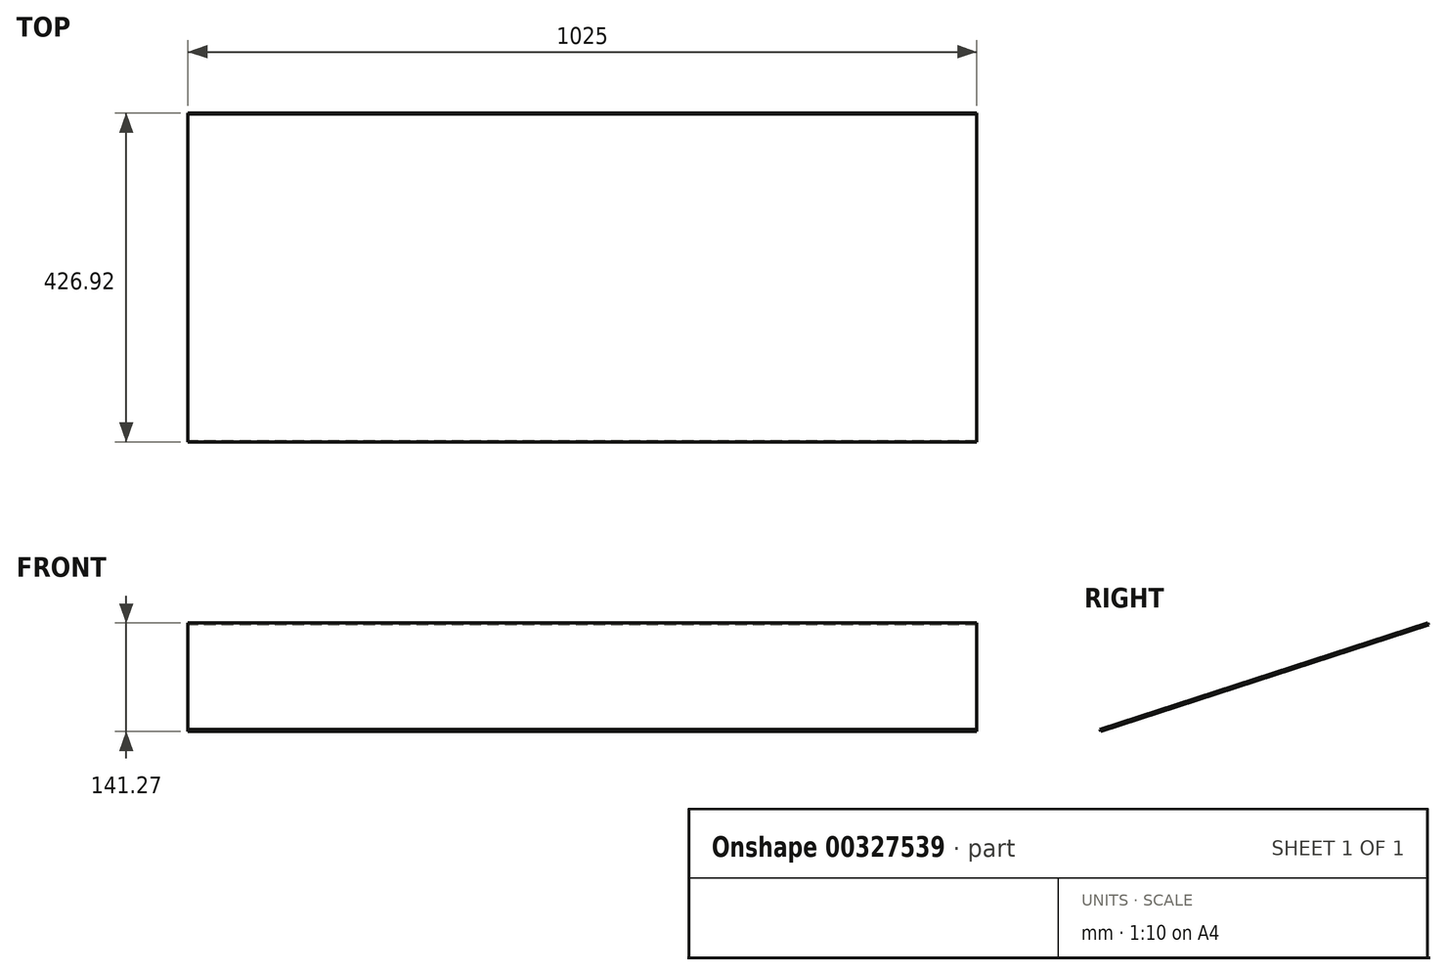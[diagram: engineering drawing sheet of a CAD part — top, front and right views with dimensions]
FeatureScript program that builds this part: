
annotation { "Feature Type Name" : "Feature", "Feature Type Description" : "" }
export const myFeature = defineFeature(function(context is Context, id is Id, definition is map)
    precondition{}
    {
        {
            var Q0;
            Q0=qCreatedBy(makeId("Right.planeOp"),FACE);
            var sketch = newSketch(context, id + "F0", { "sketchPlane" : qUnion([Q0])});
            skLineSegment(sketch, "E0", {"start": v(0, 0) * mm, "end": v(2288, 0) * mm});
            skLineSegment(sketch, "E1", {"start": v(2288, 0) * mm, "end": v(2288, 684.37) * mm});
            skLineSegment(sketch, "E2", {"start": v(2100, 0) * mm, "end": v(2100, 623.29) * mm});
            skLineSegment(sketch, "E3", {"start": v(2050, 0) * mm, "end": v(2050, 607.04) * mm});
            skLineSegment(sketch, "E4", {"start": v(2100, 623.29) * mm, "end": v(2288, 684.37) * mm});
            skLineSegment(sketch, "E5", {"start": v(2100, 623.29) * mm, "end": v(2050, 607.04) * mm});
            skLineSegment(sketch, "E6", {"start": v(2050, 607.04) * mm, "end": v(1862, 545.95) * mm});
            skLineSegment(sketch, "E7", {"start": v(2050, 607.04) * mm, "end": v(2041.35, 633.67) * mm});
            skLineSegment(sketch, "E8", {"start": v(2100, 623.29) * mm, "end": v(2091.35, 649.92) * mm});
            skLineSegment(sketch, "E9", {"start": v(2288, 684.37) * mm, "end": v(2279.35, 711) * mm});
            skLineSegment(sketch, "E10", {"start": v(2279.35, 711) * mm, "end": v(2091.35, 649.92) * mm});
            skLineSegment(sketch, "E11", {"start": v(2091.35, 649.92) * mm, "end": v(2041.35, 633.67) * mm});
            skLineSegment(sketch, "E12", {"start": v(2041.35, 633.67) * mm, "end": v(1853.35, 572.58) * mm});
            skLineSegment(sketch, "E13", {"start": v(1853.35, 572.58) * mm, "end": v(1862, 545.95) * mm});
            skLineSegment(sketch, "E14", {"start": v(1854.27, 569.73) * mm, "end": v(2280.27, 708.15) * mm});
            skSolve(sketch);
        }
        {
            var Q0;
            {var subQ0=sQuery(id+"F0.wireOp",EDGE,"0M8AAAyR-SB0r-MtMV-LE9l-MARlShi8dbRd");Q0=makeQuery(id+"F0.imprint","IMPRINT",FACE,{"disambiguationData":[TD([[makeQuery(id+"F0.imprint","IMPRINT",EDGE,{"derivedFrom":subQ0}),-1.0]])]});}
            var Q1;
            {var subQ0=sQuery(id+"F0.wireOp",EDGE,"1FGk7jgl-vVaA-wB1T-qpKy-0b2ghD9h8zY1");Q1=makeQuery(id+"F0.imprint","IMPRINT",FACE,{"disambiguationData":[TD([[makeQuery(id+"F0.imprint","IMPRINT",EDGE,{"derivedFrom":subQ0}),1.0]])]});}
            var Q2;
            {var subQ0=sQuery(id+"F0.wireOp",EDGE,"ccb0210a-ae8c-467c-bc7f-bc7526da68d5.trimOffspring");Q2=makeQuery(id+"F0.imprint","IMPRINT",FACE,{"disambiguationData":[TD([[makeQuery(id+"F0.imprint","IMPRINT",EDGE,{"derivedFrom":subQ0}),-1.0]])]});}
            var Q3;
            {var subQ0=sQuery(id+"F0.wireOp",EDGE,"E12");Q3=makeQuery(id+"F0.imprint","IMPRINT",FACE,{"disambiguationData":[TD([[makeQuery(id+"F0.imprint","IMPRINT",EDGE,{"derivedFrom":subQ0}),1.0]])]});}
            var Q4;
            {var subQ0=sQuery(id+"F0.wireOp",EDGE,"E11");Q4=makeQuery(id+"F0.imprint","IMPRINT",FACE,{"disambiguationData":[TD([[makeQuery(id+"F0.imprint","IMPRINT",EDGE,{"derivedFrom":subQ0}),1.0]])]});}
            var Q5;
            {var subQ0=sQuery(id+"F0.wireOp",EDGE,"E10");Q5=makeQuery(id+"F0.imprint","IMPRINT",FACE,{"disambiguationData":[TD([[makeQuery(id+"F0.imprint","IMPRINT",EDGE,{"derivedFrom":subQ0}),1.0]])]});}
            extrude(context, id + "F1", {"entities" : qUnion([Q0, Q1, Q2, Q3, Q4, Q5]), "depth" : 1100 * mm, "symmetric" : true});
        }
        {
            var Q0;
            Q0=makeQuery(id+"F1.opExtrude","SWEPT_FACE",FACE,{"disambiguationData":[OSD([sQuery(id+"F0.wireOp",EDGE,"E10"),sQuery(id+"F0.wireOp",EDGE,"E11"),sQuery(id+"F0.wireOp",EDGE,"E12")])]});
            var sketch = newSketch(context, id + "F2", { "sketchPlane" : qUnion([Q0])});
            skLineSegment(sketch, "E15", {"start": v(0, 2163.54) * mm, "end": v(500, 2163.54) * mm});
            skPoint(sketch, "E15.startSnap0", {"position": v(550, 2163.54) * mm});
            skPoint(sketch, "E15.startSnap1", {"position": v(0, 2387.5) * mm});
            skPoint(sketch, "E15.endSnap0", {"position": v(550, 2163.54) * mm});
            skLineSegment(sketch, "E16", {"start": v(500, 2188.54) * mm, "end": v(475, 2188.54) * mm});
            skLineSegment(sketch, "E17", {"start": v(475, 2188.54) * mm, "end": v(475, 2138.54) * mm});
            skLineSegment(sketch, "E18", {"start": v(475, 2138.54) * mm, "end": v(500, 2138.54) * mm});
            skLineSegment(sketch, "E19.bottom", {"start": v(462.5, 2387.5) * mm, "end": v(512.5, 2387.5) * mm});
            skLineSegment(sketch, "E19.top", {"start": v(462.5, 1939.58) * mm, "end": v(512.5, 1939.58) * mm});
            skLineSegment(sketch, "E19.left", {"start": v(462.5, 2387.5) * mm, "end": v(462.5, 1939.58) * mm});
            skLineSegment(sketch, "E19.right", {"start": v(512.5, 2387.5) * mm, "end": v(512.5, 1939.58) * mm});
            skPoint(sketch, "E19.middle", {"position": v(487.5, 2163.54) * mm});
            skPoint(sketch, "E19.middle.positionSnap0", {"position": v(487.5, 2138.54) * mm});
            skPoint(sketch, "E19.centerSnap0", {"position": v(487.5, 2138.54) * mm});
            skLineSegment(sketch, "E20.MirrorCS", {"start": v(0, 2163.54) * mm, "end": v(-500, 2163.54) * mm});
            skLineSegment(sketch, "E21.MirrorCS", {"start": v(-462.5, 2387.5) * mm, "end": v(-462.5, 1939.58) * mm});
            skLineSegment(sketch, "E22.MirrorCS", {"start": v(-475, 2188.54) * mm, "end": v(-475, 2138.54) * mm});
            skLineSegment(sketch, "E23.MirrorCS", {"start": v(-475, 2138.54) * mm, "end": v(-500, 2138.54) * mm});
            skLineSegment(sketch, "E24.MirrorCS", {"start": v(-500, 2138.54) * mm, "end": v(-500, 2163.54) * mm});
            skLineSegment(sketch, "E25.MirrorCS", {"start": v(-500, 2163.54) * mm, "end": v(-500, 2188.54) * mm});
            skLineSegment(sketch, "E26.MirrorCS", {"start": v(-500, 2188.54) * mm, "end": v(-475, 2188.54) * mm});
            skLineSegment(sketch, "E27.MirrorCS", {"start": v(-512.5, 2387.5) * mm, "end": v(-512.5, 1939.58) * mm});
            skLineSegment(sketch, "E28", {"start": v(500, 2138.54) * mm, "end": v(500, 2188.54) * mm});
            skSolve(sketch);
        }
        {
            var Q0;
            {var subQ0=sQuery(id+"F2.wireOp",EDGE,"E27.MirrorCS");Q0=makeQuery(id+"F2.imprint","IMPRINT",FACE,{"disambiguationData":[TD([[makeQuery(id+"F2.imprint","IMPRINT",EDGE,{"derivedFrom":subQ0}),-1.0]])]});}
            var Q1;
            {var subQ0=sQuery(id+"F2.wireOp",EDGE,"E19.right");Q1=makeQuery(id+"F2.imprint","IMPRINT",FACE,{"disambiguationData":[TD([[makeQuery(id+"F2.imprint","IMPRINT",EDGE,{"derivedFrom":subQ0}),1.0]])]});}
            extrude(context, id + "F3", {"entities" : qUnion([Q0, Q1]), "operationType" : NewBodyOperationType.REMOVE, "oppositeDirection" : true, "depth" : 25 * mm});
        }
    });
